# Revit family: S-399_Vertical
name_source: partatom
category: Plumbing Fixtures
revit_build: Autodesk Revit 2015 (Build: 20140606_1530(x64)
units: mm (PartAtom-declared; Revit-internal decimal feet)

## types (1)
- S-399_Vertical_ABS White
    Clase carga = K3
    Description = VINYL FLOOR GULLY, REMOVABLE TRAP, WITH HAIR FILTER, VERTICAL OUTLET, WITH GRID, VANDAL SAFE
    Diameter = 50 mm  [stored 0.164042 ft]
    Flowrate = 1.0 L/s
    Grid = INOX AISI304
    Hidraulic seal = 50 mm
    Manufacturer = Jimten
    Material = ABS (White)
    Model = S-399
    Outlet = 50M/110M
    Reference = 12449
    Size = Ø160 mm
    Total Minimum Height = 110 mm
    Type Comments = WITH PRESSING RING FOR VINYL WATERPROOFING MEMBRANES. WITH PROTECTION COVER
    URL = http://www.jimten.com
    WFU = 1

note: [stored X ft] marks values corroborated as IEEE doubles in the binary element streams (Revit-internal decimal feet)

## geometry (parser evidence)
native form markers: Blend x3, Sweep x7
no freeform markers — native parametric forms only
